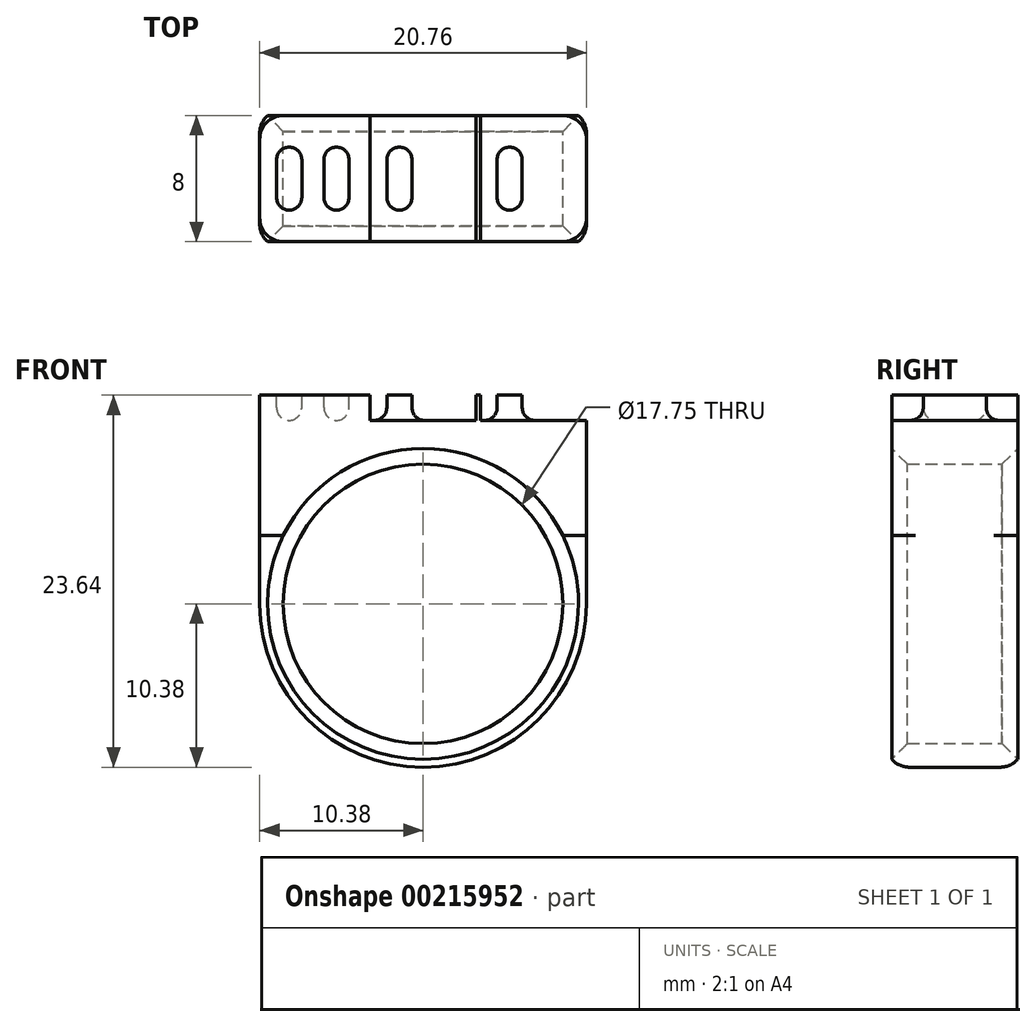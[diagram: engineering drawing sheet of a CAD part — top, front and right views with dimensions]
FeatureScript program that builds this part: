
annotation { "Feature Type Name" : "Feature", "Feature Type Description" : "" }
export const myFeature = defineFeature(function(context is Context, id is Id, definition is map)
    precondition{}
    {
        {
            var Q0;
            Q0=qCreatedBy(makeId("Front.planeOp"),FACE);
            var sketch = newSketch(context, id + "F0", { "sketchPlane" : qUnion([Q0])});
            skCircle(sketch, "E0", {"center": v(0, 0) * mm, "radius": 8.88 * mm});
            skCircle(sketch, "E1.0", {"center": v(0, 0) * mm, "radius": 10.38 * mm});
            skCircle(sketch, "E2.0", {"center": v(0, 0) * mm, "radius": 20.38 * mm});
            skLineSegment(sketch, "E3", {"start": v(10.38, 0) * mm, "end": v(10.38, 17.54) * mm});
            skLineSegment(sketch, "E4.MirrorCS", {"start": v(-10.38, 0) * mm, "end": v(-10.38, 17.54) * mm});
            skCircle(sketch, "E5.0", {"center": v(0, 0) * mm, "radius": 19.38 * mm});
            skLineSegment(sketch, "E6", {"start": v(-10.37, 13.26) * mm, "end": v(10.38, 13.26) * mm});
            skSolve(sketch);
        }
        {
            var Q0;
            Q0=makeQuery(id+"F0.imprint","IMPRINT",FACE,{"disambiguationData":[TD([[makeQuery(id+"F0.imprint","IMPRINT",EDGE,{"derivedFrom":sQuery(id+"F0.wireOp",EDGE,"E0")}),-1.0]])]});
            extrude(context, id + "F1", {"entities" : qUnion([Q0]), "depth" : 4 * mm, "hasSecondDirection" : true, "secondDirectionOppositeDirection" : true, "secondDirectionDepth" : 4 * mm});
        }
        {
            var Q0;
            Q0=makeQuery(id+"F1.opExtrude","CAP_EDGE",EDGE,{"disambiguationData":[OSD([sQuery(id+"F0.wireOp",EDGE,"E0")])],"isStart":false});
            var Q1;
            Q1=makeQuery(id+"F1.opExtrude","CAP_EDGE",EDGE,{"disambiguationData":[OSD([sQuery(id+"F0.wireOp",EDGE,"E0")])],"isStart":true});
            chamfer(context, id + "F2", {"entities" : qUnion([Q0, Q1]), "width" : 1 * mm, "tangentPropagation" : true});
        }
        {
            var Q0;
            {var subQ0=sQuery(id+"F0.wireOp",EDGE,"E3");var subQ1=sQuery(id+"F0.wireOp",EDGE,"E1.0");var subQ2=makeQuery(id+"F0.imprint","INTERSECT",VERTEX,{"derivedFrom":[subQ1,subQ0]});Q0=makeQuery(id+"F0.imprint","IMPRINT",FACE,{"disambiguationData":[TD([[makeQuery(id+"F0.imprint","IMPRINT",EDGE,{"disambiguationData":[TD([[subQ2,-1.0]])],"derivedFrom":subQ1}),-1.0]])]});}
            extrude(context, id + "F3", {"entities" : qUnion([Q0]), "operationType" : NewBodyOperationType.ADD, "depth" : 4 * mm, "hasSecondDirection" : true, "secondDirectionOppositeDirection" : true, "secondDirectionDepth" : 4 * mm});
        }
        {
            var Q0;
            {var subQ0=sQuery(id+"F0.wireOp",EDGE,"E3");var subQ1=sQuery(id+"F0.wireOp",EDGE,"E2.0");var subQ2=makeQuery(id+"F0.imprint","INTERSECT",VERTEX,{"derivedFrom":[subQ1,subQ0]});Q0=makeQuery(id+"F0.imprint","IMPRINT",FACE,{"disambiguationData":[TD([[makeQuery(id+"F0.imprint","IMPRINT",EDGE,{"disambiguationData":[TD([[subQ2,-1.0]])],"derivedFrom":subQ1}),1.0]])]});}
            extrude(context, id + "F4", {"entities" : qUnion([Q0]), "operationType" : NewBodyOperationType.REMOVE, "oppositeDirection" : true, "depth" : .5 * mm, "hasSecondDirection" : true, "secondDirectionOppositeDirection" : false, "secondDirectionDepth" : .5 * mm});
        }
        {
            var Q0;
            Q0=makeQuery(id+"F3.opExtrude","SWEPT_FACE",FACE,{"disambiguationData":[OSD([sQuery(id+"F0.wireOp",EDGE,"E6")])]});
            var sketch = newSketch(context, id + "F5", { "sketchPlane" : qUnion([Q0])});
            skLineSegment(sketch, "E7.bottom", {"start": v(1.5, 2) * mm, "end": v(1.5, 2) * mm});
            skLineSegment(sketch, "E7.top", {"start": v(1.5, -2) * mm, "end": v(1.5, -2) * mm});
            skLineSegment(sketch, "E7.left", {"start": v(0.7, 1.2) * mm, "end": v(0.7, -1.2) * mm});
            skLineSegment(sketch, "E7.right", {"start": v(2.3, 1.2) * mm, "end": v(2.3, -1.2) * mm});
            skLineSegment(sketch, "E8", {"start": v(0.7, 2) * mm, "end": v(2.3, -2) * mm, "construction": true});
            skLineSegment(sketch, "E9", {"start": v(2.3, 2) * mm, "end": v(0.7, -2) * mm, "construction": true});
            skPoint(sketch, "E10", {"position": v(1.5, 0) * mm});
            skPoint(sketch, "E11", {"position": v(3.5, 0) * mm});
            skLineSegment(sketch, "E12", {"start": v(3.5, 4) * mm, "end": v(3.5, 0) * mm, "construction": true});
            skLineSegment(sketch, "E13", {"start": v(3.5, -4) * mm, "end": v(3.5, 0) * mm, "construction": true});
            skPoint(sketch, "E14.visualSharp", {"position": v(0.7, 2) * mm});
            skArc(sketch, "E14.filletArc", {"start": v(1.5, 2) * mm, "mid": v(0.93, 1.77) * mm, "end": v(0.7, 1.2) * mm});
            skPoint(sketch, "E15.visualSharp", {"position": v(2.3, 2) * mm});
            skArc(sketch, "E15.filletArc", {"start": v(2.3, 1.2) * mm, "mid": v(2.07, 1.77) * mm, "end": v(1.5, 2) * mm});
            skPoint(sketch, "E16.visualSharp", {"position": v(2.3, -2) * mm});
            skArc(sketch, "E16.filletArc", {"start": v(1.5, -2) * mm, "mid": v(2.07, -1.77) * mm, "end": v(2.3, -1.2) * mm});
            skPoint(sketch, "E17.visualSharp", {"position": v(0.7, -2) * mm});
            skArc(sketch, "E17.filletArc", {"start": v(0.7, -1.2) * mm, "mid": v(0.93, -1.77) * mm, "end": v(1.5, -2) * mm});
            skPoint(sketch, "E18.MirrorP", {"position": v(4.7, -2) * mm});
            skLineSegment(sketch, "E19.MirrorCS", {"start": v(5.5, -2) * mm, "end": v(5.5, -2) * mm});
            skPoint(sketch, "E20.MirrorP", {"position": v(6.3, 2) * mm});
            skLineSegment(sketch, "E21.MirrorCS", {"start": v(5.5, 2) * mm, "end": v(5.5, 2) * mm});
            skPoint(sketch, "E22.MirrorP", {"position": v(6.3, -2) * mm});
            skArc(sketch, "E23.MirrorCS", {"start": v(6.3, -1.2) * mm, "mid": v(6.07, -1.77) * mm, "end": v(5.5, -2) * mm});
            skArc(sketch, "E24.MirrorCS", {"start": v(5.5, -2) * mm, "mid": v(4.93, -1.77) * mm, "end": v(4.7, -1.2) * mm});
            skPoint(sketch, "E25.MirrorP", {"position": v(5.5, 0) * mm});
            skLineSegment(sketch, "E26.MirrorCS", {"start": v(4.7, 2) * mm, "end": v(6.3, -2) * mm, "construction": true});
            skArc(sketch, "E27.MirrorCS", {"start": v(4.7, 1.2) * mm, "mid": v(4.93, 1.77) * mm, "end": v(5.5, 2) * mm});
            skPoint(sketch, "E28.MirrorP", {"position": v(4.7, 2) * mm});
            skLineSegment(sketch, "E29.MirrorCS", {"start": v(6.3, 2) * mm, "end": v(4.7, -2) * mm, "construction": true});
            skLineSegment(sketch, "E30.MirrorCS", {"start": v(6.3, 1.2) * mm, "end": v(6.3, -1.2) * mm});
            skLineSegment(sketch, "E31.MirrorCS", {"start": v(4.7, 1.2) * mm, "end": v(4.7, -1.2) * mm});
            skArc(sketch, "E32.MirrorCS", {"start": v(5.5, 2) * mm, "mid": v(6.07, 1.77) * mm, "end": v(6.3, 1.2) * mm});
            skPoint(sketch, "E33.MirrorP", {"position": v(-2.3, -2) * mm});
            skLineSegment(sketch, "E34.MirrorCS", {"start": v(-5.5, 2) * mm, "end": v(-5.5, 2) * mm});
            skLineSegment(sketch, "E35.MirrorCS", {"start": v(-4.7, 2) * mm, "end": v(-6.3, -2) * mm, "construction": true});
            skPoint(sketch, "E36.MirrorP", {"position": v(-0.7, -2) * mm});
            skArc(sketch, "E37.MirrorCS", {"start": v(-5.5, -2) * mm, "mid": v(-4.93, -1.77) * mm, "end": v(-4.7, -1.2) * mm});
            skArc(sketch, "E38.MirrorCS", {"start": v(-6.3, -1.2) * mm, "mid": v(-6.07, -1.77) * mm, "end": v(-5.5, -2) * mm});
            skArc(sketch, "E39.MirrorCS", {"start": v(-0.7, -1.2) * mm, "mid": v(-0.93, -1.77) * mm, "end": v(-1.5, -2) * mm});
            skArc(sketch, "E40.MirrorCS", {"start": v(-1.5, -2) * mm, "mid": v(-2.07, -1.77) * mm, "end": v(-2.3, -1.2) * mm});
            skArc(sketch, "E41.MirrorCS", {"start": v(-2.3, 1.2) * mm, "mid": v(-2.07, 1.77) * mm, "end": v(-1.5, 2) * mm});
            skArc(sketch, "E42.MirrorCS", {"start": v(-1.5, 2) * mm, "mid": v(-0.93, 1.77) * mm, "end": v(-0.7, 1.2) * mm});
            skLineSegment(sketch, "E43.MirrorCS", {"start": v(-2.3, 2) * mm, "end": v(-0.7, -2) * mm, "construction": true});
            skLineSegment(sketch, "E44.MirrorCS", {"start": v(-0.7, 2) * mm, "end": v(-2.3, -2) * mm, "construction": true});
            skArc(sketch, "E45.MirrorCS", {"start": v(-5.5, 2) * mm, "mid": v(-6.07, 1.77) * mm, "end": v(-6.3, 1.2) * mm});
            skPoint(sketch, "E46.MirrorP", {"position": v(-2.3, 2) * mm});
            skArc(sketch, "E47.MirrorCS", {"start": v(-4.7, 1.2) * mm, "mid": v(-4.93, 1.77) * mm, "end": v(-5.5, 2) * mm});
            skPoint(sketch, "E48.MirrorP", {"position": v(-0.7, 2) * mm});
            skLineSegment(sketch, "E49.MirrorCS", {"start": v(-2.3, 1.2) * mm, "end": v(-2.3, -1.2) * mm});
            skLineSegment(sketch, "E50.MirrorCS", {"start": v(-1.5, -2) * mm, "end": v(-1.5, -2) * mm});
            skPoint(sketch, "E51.MirrorP", {"position": v(-5.5, 0) * mm});
            skPoint(sketch, "E52.MirrorP", {"position": v(-6.3, 2) * mm});
            skPoint(sketch, "E53.MirrorP", {"position": v(-1.5, 0) * mm});
            skLineSegment(sketch, "E54.MirrorCS", {"start": v(-6.3, 2) * mm, "end": v(-4.7, -2) * mm, "construction": true});
            skLineSegment(sketch, "E55.MirrorCS", {"start": v(-0.7, 1.2) * mm, "end": v(-0.7, -1.2) * mm});
            skPoint(sketch, "E56.MirrorP", {"position": v(-6.3, -2) * mm});
            skPoint(sketch, "E57.MirrorP", {"position": v(-4.7, 2) * mm});
            skLineSegment(sketch, "E58.MirrorCS", {"start": v(-5.5, -2) * mm, "end": v(-5.5, -2) * mm});
            skPoint(sketch, "E59.MirrorP", {"position": v(-3.5, 0) * mm});
            skLineSegment(sketch, "E60.MirrorCS", {"start": v(-1.5, 2) * mm, "end": v(-1.5, 2) * mm});
            skLineSegment(sketch, "E61.MirrorCS", {"start": v(-4.7, 1.2) * mm, "end": v(-4.7, -1.2) * mm});
            skLineSegment(sketch, "E62.MirrorCS", {"start": v(-6.3, 1.2) * mm, "end": v(-6.3, -1.2) * mm});
            skPoint(sketch, "E63.MirrorP", {"position": v(-4.7, -2) * mm});
            skPoint(sketch, "E64", {"position": v(-10.38, 4) * mm});
            skPoint(sketch, "E65", {"position": v(10.38, 4) * mm});
            skPoint(sketch, "E66", {"position": v(7, 0) * mm});
            skLineSegment(sketch, "E67", {"start": v(7, -4) * mm, "end": v(7, 0) * mm, "construction": true});
            skLineSegment(sketch, "E68.MirrorCS", {"start": v(8.5, -2) * mm, "end": v(8.5, -2) * mm});
            skLineSegment(sketch, "E69.MirrorCS", {"start": v(8.5, 2) * mm, "end": v(8.5, 2) * mm});
            skPoint(sketch, "E70.MirrorP", {"position": v(9.3, 2) * mm});
            skPoint(sketch, "E71.MirrorP", {"position": v(9.3, -2) * mm});
            skLineSegment(sketch, "E72.MirrorCS", {"start": v(9.3, 1.2) * mm, "end": v(9.3, -1.2) * mm});
            skPoint(sketch, "E73.MirrorP", {"position": v(8.5, 0) * mm});
            skArc(sketch, "E74.MirrorCS", {"start": v(9.3, 1.2) * mm, "mid": v(9.07, 1.77) * mm, "end": v(8.5, 2) * mm});
            skPoint(sketch, "E75.MirrorP", {"position": v(7.7, 2) * mm});
            skArc(sketch, "E76.MirrorCS", {"start": v(8.5, 2) * mm, "mid": v(7.93, 1.77) * mm, "end": v(7.7, 1.2) * mm});
            skLineSegment(sketch, "E77.MirrorCS", {"start": v(9.3, 2) * mm, "end": v(7.7, -2) * mm, "construction": true});
            skLineSegment(sketch, "E78.MirrorCS", {"start": v(7.7, 1.2) * mm, "end": v(7.7, -1.2) * mm});
            skArc(sketch, "E79.MirrorCS", {"start": v(7.7, -1.2) * mm, "mid": v(7.93, -1.77) * mm, "end": v(8.5, -2) * mm});
            skArc(sketch, "E80.MirrorCS", {"start": v(8.5, -2) * mm, "mid": v(9.07, -1.77) * mm, "end": v(9.3, -1.2) * mm});
            skPoint(sketch, "E81.MirrorP", {"position": v(7.7, -2) * mm});
            skLineSegment(sketch, "E82.MirrorCS", {"start": v(7.7, 2) * mm, "end": v(9.3, -2) * mm, "construction": true});
            skLineSegment(sketch, "E83.MirrorCS", {"start": v(-8.5, 2) * mm, "end": v(-8.5, 2) * mm});
            skLineSegment(sketch, "E84.MirrorCS", {"start": v(-8.5, -2) * mm, "end": v(-8.5, -2) * mm});
            skLineSegment(sketch, "E85.MirrorCS", {"start": v(-9.3, 2) * mm, "end": v(-7.7, -2) * mm, "construction": true});
            skPoint(sketch, "E86.MirrorP", {"position": v(-7.7, 2) * mm});
            skLineSegment(sketch, "E87.MirrorCS", {"start": v(-7.7, 1.2) * mm, "end": v(-7.7, -1.2) * mm});
            skLineSegment(sketch, "E88.MirrorCS", {"start": v(-7.7, 2) * mm, "end": v(-9.3, -2) * mm, "construction": true});
            skLineSegment(sketch, "E89.MirrorCS", {"start": v(-9.3, 1.2) * mm, "end": v(-9.3, -1.2) * mm});
            skPoint(sketch, "E90.MirrorP", {"position": v(-8.5, 0) * mm});
            skArc(sketch, "E91.MirrorCS", {"start": v(-9.3, 1.2) * mm, "mid": v(-9.07, 1.77) * mm, "end": v(-8.5, 2) * mm});
            skArc(sketch, "E92.MirrorCS", {"start": v(-7.7, -1.2) * mm, "mid": v(-7.93, -1.77) * mm, "end": v(-8.5, -2) * mm});
            skArc(sketch, "E93.MirrorCS", {"start": v(-8.5, 2) * mm, "mid": v(-7.93, 1.77) * mm, "end": v(-7.7, 1.2) * mm});
            skPoint(sketch, "E94.MirrorP", {"position": v(-9.3, 2) * mm});
            skArc(sketch, "E95.MirrorCS", {"start": v(-8.5, -2) * mm, "mid": v(-9.07, -1.77) * mm, "end": v(-9.3, -1.2) * mm});
            skPoint(sketch, "E96.MirrorP", {"position": v(-9.3, -2) * mm});
            skPoint(sketch, "E97.MirrorP", {"position": v(-7.7, -2) * mm});
            skLineSegment(sketch, "E98", {"start": v(3.35, 4) * mm, "end": v(3.35, -4) * mm});
            skLineSegment(sketch, "E99.MirrorCS", {"start": v(3.65, 4) * mm, "end": v(3.65, -4) * mm});
            skLineSegment(sketch, "E100", {"start": v(3.35, 4) * mm, "end": v(3.65, 4) * mm});
            skLineSegment(sketch, "E101", {"start": v(3.35, -4) * mm, "end": v(3.65, -4) * mm});
            skLineSegment(sketch, "E102.MirrorCS", {"start": v(-3.35, 4) * mm, "end": v(-3.65, 4) * mm});
            skLineSegment(sketch, "E103.MirrorCS", {"start": v(-3.35, -4) * mm, "end": v(-3.65, -4) * mm});
            skLineSegment(sketch, "E104.MirrorCS", {"start": v(-3.35, 4) * mm, "end": v(-3.35, -4) * mm});
            skLineSegment(sketch, "E105.MirrorCS", {"start": v(-3.65, 4) * mm, "end": v(-3.65, -4) * mm});
            skLineSegment(sketch, "E106.MirrorCS", {"start": v(-3.5, -4) * mm, "end": v(-3.5, 0) * mm, "construction": true});
            skLineSegment(sketch, "E107.MirrorCS", {"start": v(-3.5, 4) * mm, "end": v(-3.5, 0) * mm, "construction": true});
            skSolve(sketch);
        }
        {
            var Q0;
            Q0=makeQuery(id+"F5.imprint","IMPRINT",FACE,{"disambiguationData":[TD([[makeQuery(id+"F5.imprint","IMPRINT",EDGE,{"derivedFrom":sQuery(id+"F5.wireOp",EDGE,"E72.MirrorCS")}),-1.0]])]});
            var Q1;
            Q1=makeQuery(id+"F5.imprint","IMPRINT",FACE,{"disambiguationData":[TD([[makeQuery(id+"F5.imprint","IMPRINT",EDGE,{"derivedFrom":sQuery(id+"F5.wireOp",EDGE,"E23.MirrorCS")}),-1.0]])]});
            var Q2;
            Q2=makeQuery(id+"F5.imprint","IMPRINT",FACE,{"disambiguationData":[TD([[makeQuery(id+"F5.imprint","IMPRINT",EDGE,{"derivedFrom":sQuery(id+"F5.wireOp",EDGE,"E7.left")}),1.0]])]});
            var Q3;
            Q3=makeQuery(id+"F5.imprint","IMPRINT",FACE,{"disambiguationData":[TD([[makeQuery(id+"F5.imprint","IMPRINT",EDGE,{"derivedFrom":sQuery(id+"F5.wireOp",EDGE,"E39.MirrorCS")}),-1.0]])]});
            var Q4;
            Q4=makeQuery(id+"F5.imprint","IMPRINT",FACE,{"disambiguationData":[TD([[makeQuery(id+"F5.imprint","IMPRINT",EDGE,{"derivedFrom":sQuery(id+"F5.wireOp",EDGE,"E37.MirrorCS")}),1.0]])]});
            var Q5;
            Q5=makeQuery(id+"F5.imprint","IMPRINT",FACE,{"disambiguationData":[TD([[makeQuery(id+"F5.imprint","IMPRINT",EDGE,{"derivedFrom":sQuery(id+"F5.wireOp",EDGE,"E87.MirrorCS")}),-1.0]])]});
            extrude(context, id + "F6", {"entities" : qUnion([Q0, Q1, Q2, Q3, Q4, Q5]), "operationType" : NewBodyOperationType.REMOVE, "oppositeDirection" : true, "depth" : 1.6 * mm});
        }
        {
            var Q0;
            Q0=makeQuery(id+"F6.boolean.opBoolean","COPY",EDGE,{"derivedFrom":makeQuery(id+"F6.opExtrude","CAP_EDGE",EDGE,{"disambiguationData":[OSD([sQuery(id+"F5.wireOp",EDGE,"E74.MirrorCS"),sQuery(id+"F5.wireOp",EDGE,"E76.MirrorCS")])],"isStart":false})});
            var Q1;
            Q1=makeQuery(id+"F6.boolean.opBoolean","COPY",EDGE,{"derivedFrom":makeQuery(id+"F6.opExtrude","CAP_EDGE",EDGE,{"disambiguationData":[OSD([sQuery(id+"F5.wireOp",EDGE,"E27.MirrorCS"),sQuery(id+"F5.wireOp",EDGE,"E32.MirrorCS")])],"isStart":false})});
            var Q2;
            Q2=makeQuery(id+"F6.boolean.opBoolean","COPY",EDGE,{"derivedFrom":makeQuery(id+"F6.opExtrude","CAP_EDGE",EDGE,{"disambiguationData":[OSD([sQuery(id+"F5.wireOp",EDGE,"E14.filletArc"),sQuery(id+"F5.wireOp",EDGE,"E15.filletArc")])],"isStart":false})});
            var Q3;
            Q3=makeQuery(id+"F6.boolean.opBoolean","COPY",EDGE,{"derivedFrom":makeQuery(id+"F6.opExtrude","CAP_EDGE",EDGE,{"disambiguationData":[OSD([sQuery(id+"F5.wireOp",EDGE,"E41.MirrorCS"),sQuery(id+"F5.wireOp",EDGE,"E42.MirrorCS")])],"isStart":false})});
            var Q4;
            Q4=makeQuery(id+"F6.boolean.opBoolean","COPY",EDGE,{"derivedFrom":makeQuery(id+"F6.opExtrude","CAP_EDGE",EDGE,{"disambiguationData":[OSD([sQuery(id+"F5.wireOp",EDGE,"E45.MirrorCS"),sQuery(id+"F5.wireOp",EDGE,"E47.MirrorCS")])],"isStart":false})});
            var Q5;
            Q5=makeQuery(id+"F6.boolean.opBoolean","COPY",EDGE,{"derivedFrom":makeQuery(id+"F6.opExtrude","CAP_EDGE",EDGE,{"disambiguationData":[OSD([sQuery(id+"F5.wireOp",EDGE,"E91.MirrorCS"),sQuery(id+"F5.wireOp",EDGE,"E93.MirrorCS")])],"isStart":false})});
            fillet(context, id + "F7", {"entities" : qUnion([Q0, Q1, Q2, Q3, Q4, Q5]), "radius" : (1.6 / 2) * mm, "tangentPropagation" : true, "allowEdgeOverflow" : false});
        }
        {
            var Q0;
            Q0=makeQuery(id+"F3.opExtrude","CAP_EDGE",EDGE,{"disambiguationData":[OSD([sQuery(id+"F0.wireOp",EDGE,"E3")])],"isStart":true});
            var Q1;
            Q1=makeQuery(id+"F3.opExtrude","CAP_EDGE",EDGE,{"disambiguationData":[OSD([sQuery(id+"F0.wireOp",EDGE,"E4.MirrorCS")])],"isStart":false});
            fillet(context, id + "F8", {"entities" : qUnion([Q0, Q1]), "radius" : 1.5 * mm, "tangentPropagation" : true, "allowEdgeOverflow" : false});
        }
    });
